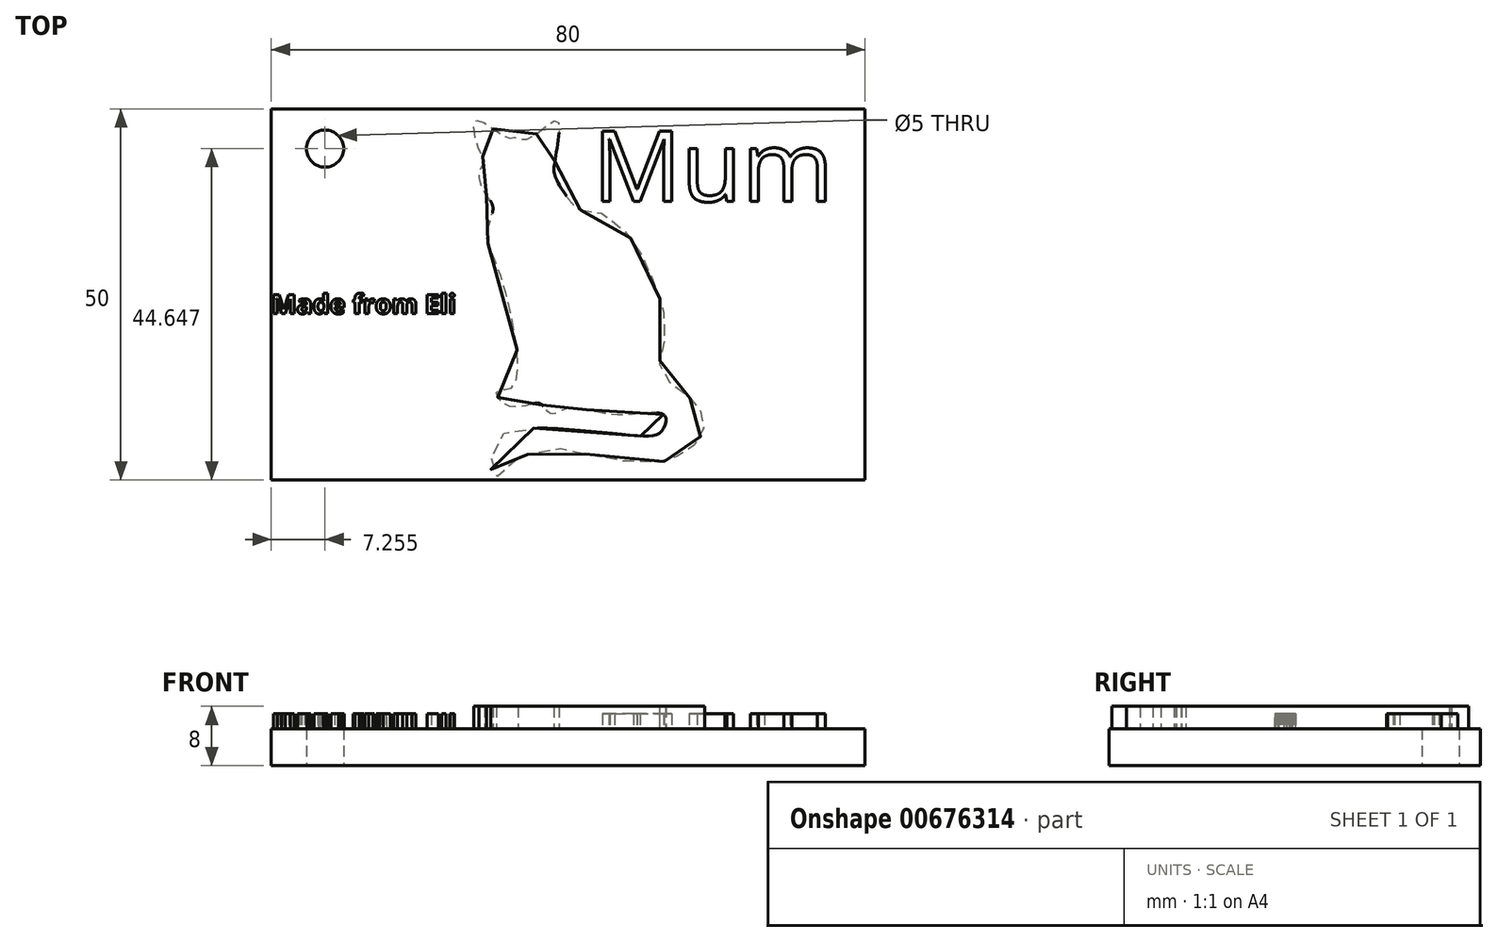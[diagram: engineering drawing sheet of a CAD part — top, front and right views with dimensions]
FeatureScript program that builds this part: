
annotation { "Feature Type Name" : "Feature", "Feature Type Description" : "" }
export const myFeature = defineFeature(function(context is Context, id is Id, definition is map)
    precondition{}
    {
        {
            var Q0;
            Q0=qCreatedBy(makeId("Top.planeOp"),FACE);
            var sketch = newSketch(context, id + "F0", { "sketchPlane" : qUnion([Q0])});
            skPoint(sketch, "E0.middle", {"position": v(0, 0) * mm});
            skFitSpline(sketch, "E1", {"points": [v(1.66, 11.36) * mm, v(4.5, 10.94) * mm, v(8.71, 7.26) * mm, v(10.81, 3.37) * mm, v(13.02, -3.15) * mm, v(12.7, -7.36) * mm, v(12.5, -10.62) * mm, v(15.13, -12.73) * mm, v(17.02, -14.73) * mm, v(18.28, -16.52) * mm, v(18.07, -18.62) * mm, v(16.7, -20.62) * mm, v(14.4, -21.99) * mm, v(11.97, -22.62) * mm, v(3.35, -21.78) * mm, v(-1.28, -20.83) * mm, v(-5.28, -21.57) * mm, v(-6.65, -21.99) * mm, v(-9.91, -24.62) * mm, v(-9.91, -20.3) * mm, v(-6.44, -18.1) * mm, v(8.08, -18.94) * mm, v(12.08, -18.83) * mm, v(13.02, -17.67) * mm, v(12.92, -16.2) * mm, v(6.4, -16.2) * mm, v(0, -15.36) * mm, v(-2.34, -16.1) * mm, v(-3.7, -14.73) * mm, v(-6.23, -15.15) * mm, v(-9.17, -14.3) * mm, v(-9.5, -12.94) * mm, v(-7.39, -12.41) * mm, v(-9.38, 3.37) * mm, v(-10.96, 8.2) * mm, v(-10.12, 11.68) * mm, v(-11.28, 13.78) * mm, v(-11.9, 16.73) * mm, v(-11.28, 17.89) * mm, v(-12.02, 19.57) * mm, v(-12.33, 23.44) * mm, v(-8.33, 21.15) * mm, v(-7.28, 21.15) * mm, v(-5.39, 20.94) * mm, v(-1.5, 23.44) * mm, v(-1.81, 17.78) * mm, v(-1.5, 15.36) * mm, v(1.66, 11.36) * mm]});
            skLineSegment(sketch, "E2.bottom", {"start": v(-40, -25) * mm, "end": v(40, -25) * mm});
            skLineSegment(sketch, "E2.top", {"start": v(-40, 25) * mm, "end": v(40, 25) * mm});
            skLineSegment(sketch, "E2.left", {"start": v(-40, -25) * mm, "end": v(-40, 25) * mm});
            skLineSegment(sketch, "E2.right", {"start": v(40, -25) * mm, "end": v(40, 25) * mm});
            skCircle(sketch, "E3", {"center": v(-32.75, 19.65) * mm, "radius": 2.5 * mm});
            skSolve(sketch);
        }
        {
            var Q0;
            Q0=makeQuery(id+"F0.imprint","IMPRINT",FACE,{"disambiguationData":[TD([[makeQuery(id+"F0.imprint","IMPRINT",EDGE,{"derivedFrom":sQuery(id+"F0.wireOp",EDGE,"E1")}),1.0]])]});
            extrude(context, id + "F1", {"entities" : qUnion([Q0]), "depth" : 5 * mm, "offsetDistance" : 25 * mm});
        }
        {
            var Q0;
            Q0=makeQuery(id+"F0.imprint","IMPRINT",FACE,{"disambiguationData":[TD([[makeQuery(id+"F0.imprint","IMPRINT",EDGE,{"derivedFrom":sQuery(id+"F0.wireOp",EDGE,"E1")}),-1.0]])]});
            extrude(context, id + "F2", {"entities" : qUnion([Q0]), "operationType" : NewBodyOperationType.ADD, "depth" : 8 * mm, "offsetDistance" : 25 * mm});
        }
        {
            var Q0;
            Q0=makeQuery(id+"F1.opExtrude","CAP_FACE",FACE,{"disambiguationData":[OSD([sQuery(id+"F0.wireOp",EDGE,"E1"),sQuery(id+"F0.wireOp",EDGE,"E2.bottom"),sQuery(id+"F0.wireOp",EDGE,"E2.top"),sQuery(id+"F0.wireOp",EDGE,"E2.left"),sQuery(id+"F0.wireOp",EDGE,"E2.right"),sQuery(id+"F0.wireOp",EDGE,"E3")])],"isStart":false});
            var sketch = newSketch(context, id + "F3", { "sketchPlane" : qUnion([Q0])});
            skText(sketch, "E4", { "text": "Mum", "fontName": "OpenSans-Regular.ttf"});
            const initialGuessF3  = {"E4": [0.00331, 0.01253, 1, 0, 0.00954]};
            skSetInitialGuess(sketch, initialGuessF3);
            skSolve(sketch);
        }
        {
            var Q0;
            Q0 = qSketchRegion(id + "F3", true);
            extrude(context, id + "F4", {"entities" : qUnion([Q0]), "operationType" : NewBodyOperationType.ADD, "depth" : 2 * mm, "offsetDistance" : 25 * mm});
        }
        {
            var Q0;
            Q0=makeQuery(id+"F1.opExtrude","CAP_FACE",FACE,{"disambiguationData":[OSD([sQuery(id+"F0.wireOp",EDGE,"E1"),sQuery(id+"F0.wireOp",EDGE,"E2.bottom"),sQuery(id+"F0.wireOp",EDGE,"E2.top"),sQuery(id+"F0.wireOp",EDGE,"E2.left"),sQuery(id+"F0.wireOp",EDGE,"E2.right"),sQuery(id+"F0.wireOp",EDGE,"E3")])],"isStart":false});
            var sketch = newSketch(context, id + "F5", { "sketchPlane" : qUnion([Q0])});
            skText(sketch, "E5", { "text": "Made from Eli", "fontName": "OpenSans-Bold.ttf"});
            const initialGuessF5  = {"E5": [-0.04, -0.0026, 1, 0, 0.0026]};
            skSetInitialGuess(sketch, initialGuessF5);
            skSolve(sketch);
        }
        {
            var Q0;
            Q0 = qSketchRegion(id + "F5", true);
            extrude(context, id + "F6", {"entities" : qUnion([Q0]), "operationType" : NewBodyOperationType.ADD, "depth" : 2 * mm, "offsetDistance" : 25 * mm});
        }
    });
